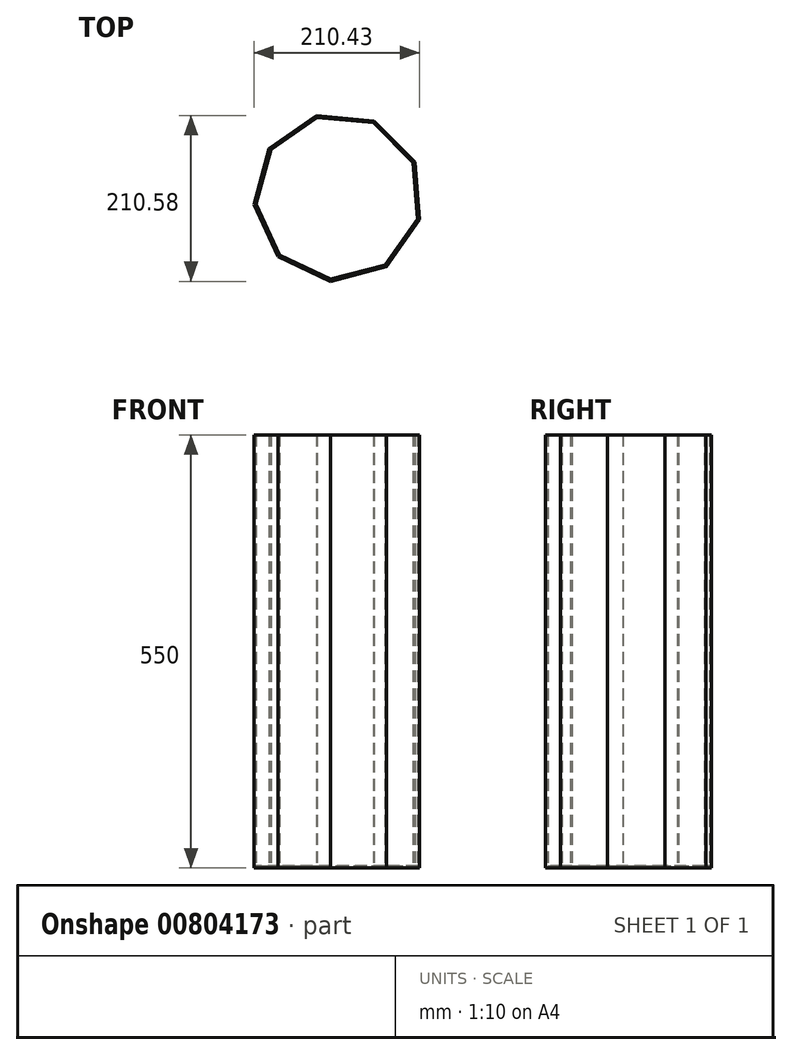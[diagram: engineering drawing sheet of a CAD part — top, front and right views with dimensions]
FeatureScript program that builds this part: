
annotation { "Feature Type Name" : "Feature", "Feature Type Description" : "" }
export const myFeature = defineFeature(function(context is Context, id is Id, definition is map)
    precondition{}
    {
        {
            var Q0;
            Q0=qCreatedBy(makeId("Top.planeOp"),FACE);
            var sketch = newSketch(context, id + "F0", { "sketchPlane" : qUnion([Q0])});
            skCircle(sketch, "E0.cCircle", {"center": v(0, 0) * mm, "radius": 100.81 * mm, "construction": true});
            skLineSegment(sketch, "E0.0", {"start": v(61.19, -88.12) * mm, "end": v(-9.77, -106.84) * mm});
            skLineSegment(sketch, "E0.1", {"start": v(-9.77, -106.84) * mm, "end": v(-76.16, -75.56) * mm});
            skLineSegment(sketch, "E0.2", {"start": v(-76.16, -75.56) * mm, "end": v(-106.91, -8.93) * mm});
            skLineSegment(sketch, "E0.3", {"start": v(-106.91, -8.93) * mm, "end": v(-87.64, 61.88) * mm});
            skLineSegment(sketch, "E0.4", {"start": v(-87.64, 61.88) * mm, "end": v(-27.36, 103.74) * mm});
            skLineSegment(sketch, "E0.5", {"start": v(-27.36, 103.74) * mm, "end": v(45.72, 97.05) * mm});
            skLineSegment(sketch, "E0.6", {"start": v(45.72, 97.05) * mm, "end": v(97.4, 44.95) * mm});
            skLineSegment(sketch, "E0.7", {"start": v(97.4, 44.95) * mm, "end": v(103.52, -28.18) * mm});
            skLineSegment(sketch, "E0.8", {"start": v(103.52, -28.18) * mm, "end": v(61.19, -88.12) * mm});
            skPoint(sketch, "E0.0.midPoint", {"position": v(25.7, -97.48) * mm});
            skSolve(sketch);
        }
        {
            var Q0;
            Q0 = qSketchRegion(id + "F0", true);
            extrude(context, id + "F1", {"entities" : qUnion([Q0]), "depth" : 550 * mm, "offsetDistance" : 25.4 * mm});
        }
        {
            var Q0;
            Q0=makeQuery(id+"F1.opExtrude","CAP_FACE",FACE,{"disambiguationData":[OSD([sQuery(id+"F0.wireOp",EDGE,"E0.0"),sQuery(id+"F0.wireOp",EDGE,"E0.1"),sQuery(id+"F0.wireOp",EDGE,"E0.2"),sQuery(id+"F0.wireOp",EDGE,"E0.3"),sQuery(id+"F0.wireOp",EDGE,"E0.4"),sQuery(id+"F0.wireOp",EDGE,"E0.5"),sQuery(id+"F0.wireOp",EDGE,"E0.6"),sQuery(id+"F0.wireOp",EDGE,"E0.7"),sQuery(id+"F0.wireOp",EDGE,"E0.8")])],"isStart":false});
            shell(context, id + "F2", {"entities" : qUnion([Q0]), "thickness" : 2.54 * mm});
        }
    });
